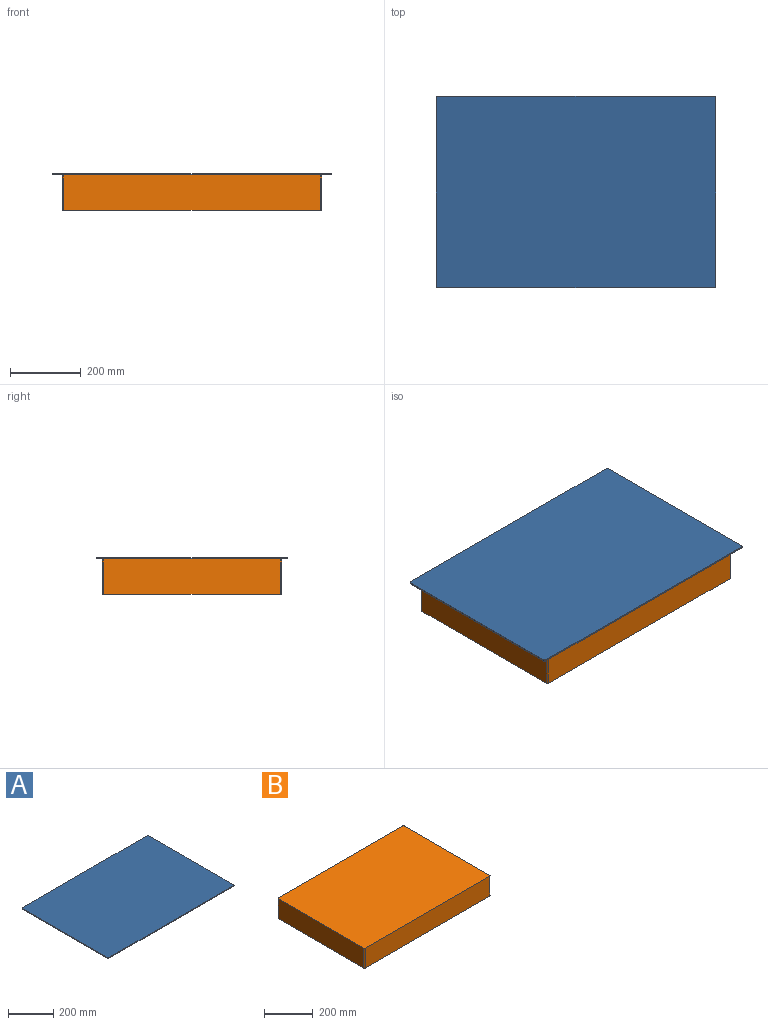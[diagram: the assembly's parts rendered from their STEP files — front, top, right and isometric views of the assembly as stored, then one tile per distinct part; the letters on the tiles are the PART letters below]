
ASSEMBLY  parts=2 mates=3
PART A: 10 faces, bbox 788x540x4 mm
  f0: plane 532x4mm, normal (1,0,0), area 2128mm2, adj f4,f5,f6,f9
  f1: plane 780x4mm, normal (0,1,0), area 3120mm2, adj f4,f5,f6,f7
  f2: plane 532x4mm, normal (-1,0,0), area 2128mm2, adj f4,f5,f7,f8
  f3: plane 780x4mm, normal (0,-1,0), area 3120mm2, adj f4,f5,f8,f9
  f4: plane 788x540mm, normal (0,0,1), area 425506.3mm2, adj f0,f1,f2,f3,f6,f7,f8,f9
  f5: plane 788x540mm, normal (0,0,-1), area 425506.3mm2, adj f0,f1,f2,f3,f6,f7,f8,f9
  f6: cylinder r=4mm len=4mm, axis (0,0,1), area 25.1mm2, adj f0,f1,f4,f5
  f7: cylinder r=4mm len=4mm, axis (0,0,-1), area 25.1mm2, adj f1,f2,f4,f5
  f8: cylinder r=4mm len=4mm, axis (0,0,1), area 25.1mm2, adj f2,f3,f4,f5
  f9: cylinder r=4mm len=4mm, axis (0,0,-1), area 25.1mm2, adj f0,f3,f4,f5
PART B: 10 faces, bbox 731x505x100 mm
  f0: plane 497x100mm, normal (1,0,0), area 49700mm2, adj f4,f5,f6,f9
  f1: plane 723x100mm, normal (0,1,0), area 72300mm2, adj f4,f5,f6,f7
  f2: plane 497x100mm, normal (-1,0,0), area 49700mm2, adj f4,f5,f7,f8
  f3: plane 723x100mm, normal (0,-1,0), area 72300mm2, adj f4,f5,f8,f9
  f4: plane 731x505mm, normal (0,0,-1), area 369141.3mm2, adj f0,f1,f2,f3,f6,f7,f8,f9
  f5: plane 731x505mm, normal (0,0,1), area 369141.3mm2, adj f0,f1,f2,f3,f6,f7,f8,f9
  f6: cylinder r=4mm len=100mm, axis (0,0,-1), area 628.3mm2, adj f0,f1,f4,f5
  f7: cylinder r=4mm len=100mm, axis (0,0,1), area 628.3mm2, adj f1,f2,f4,f5
  f8: cylinder r=4mm len=100mm, axis (0,0,-1), area 628.3mm2, adj f2,f3,f4,f5
  f9: cylinder r=4mm len=100mm, axis (0,0,1), area 628.3mm2, adj f0,f3,f4,f5
PLACE A t=(336.39,125.75,-130.24)mm
PLACE B t=(336.39,125.75,-130.24)mm
MATE parallel B.f3 <-> A.f3  axis (0,-1,0) through (336.39,-126.75,-180.24)mm
MATE parallel A.f5 <-> B.f4  axis (0,0,-1) through (336.39,125.75,-130.24)mm
MATE parallel A.f2 <-> B.f2  axis (-1,0,0) through (-57.61,125.75,-128.24)mm
